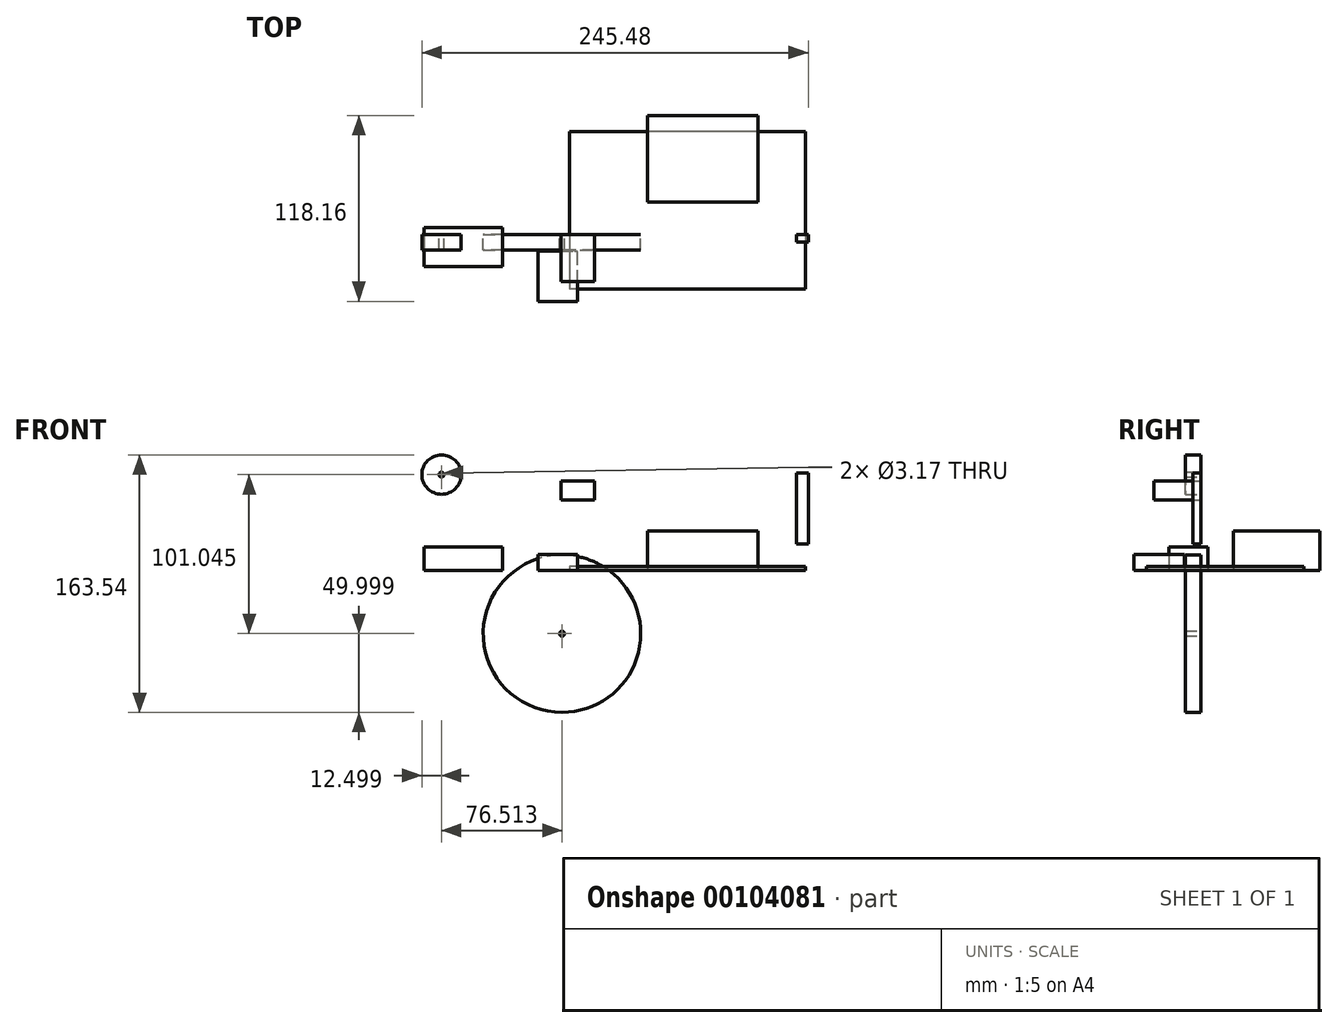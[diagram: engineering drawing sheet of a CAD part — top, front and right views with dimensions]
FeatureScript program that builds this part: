
annotation { "Feature Type Name" : "Feature", "Feature Type Description" : "" }
export const myFeature = defineFeature(function(context is Context, id is Id, definition is map)
    precondition{}
    {
        {
            var Q0;
            Q0=qCreatedBy(makeId("Top.planeOp"),FACE);
            var sketch = newSketch(context, id + "F0", { "sketchPlane" : qUnion([Q0])});
            skLineSegment(sketch, "E0.bottom", {"start": v(-136.78, 4.5) * mm, "end": v(-86.78, 4.5) * mm});
            skLineSegment(sketch, "E0.top", {"start": v(-136.78, -20.5) * mm, "end": v(-86.78, -20.5) * mm});
            skLineSegment(sketch, "E0.left", {"start": v(-136.78, 4.5) * mm, "end": v(-136.78, -20.5) * mm});
            skLineSegment(sketch, "E0.right", {"start": v(-86.78, 4.5) * mm, "end": v(-86.78, -20.5) * mm});
            skSolve(sketch);
        }
        {
            var Q0;
            Q0=makeQuery(id+"F0.imprint","IMPRINT",FACE,{"disambiguationData":[TD([[makeQuery(id+"F0.imprint","IMPRINT",EDGE,{"derivedFrom":sQuery(id+"F0.wireOp",EDGE,"E0.bottom")}),-1.0]])]});
            extrude(context, id + "F1", {"entities" : qUnion([Q0]), "depth" : 15 * mm});
        }
        {
            var Q0;
            Q0=qCreatedBy(makeId("Top.planeOp"),FACE);
            var sketch = newSketch(context, id + "F2", { "sketchPlane" : qUnion([Q0])});
            skLineSegment(sketch, "E1.bottom", {"start": v(5.38, 75.6) * mm, "end": v(75.38, 75.6) * mm});
            skLineSegment(sketch, "E1.top", {"start": v(5.38, 20.6) * mm, "end": v(75.38, 20.6) * mm});
            skLineSegment(sketch, "E1.left", {"start": v(5.38, 75.6) * mm, "end": v(5.38, 20.6) * mm});
            skLineSegment(sketch, "E1.right", {"start": v(75.38, 75.6) * mm, "end": v(75.38, 20.6) * mm});
            skSolve(sketch);
        }
        {
            var Q0;
            Q0=makeQuery(id+"F2.imprint","IMPRINT",FACE,{"disambiguationData":[TD([[makeQuery(id+"F2.imprint","IMPRINT",EDGE,{"derivedFrom":sQuery(id+"F2.wireOp",EDGE,"E1.bottom")}),-1.0]])]});
            extrude(context, id + "F3", {"entities" : qUnion([Q0]), "depth" : 25 * mm});
        }
        {
            var Q0;
            Q0=qCreatedBy(makeId("Front.planeOp"),FACE);
            var sketch = newSketch(context, id + "F4", { "sketchPlane" : qUnion([Q0])});
            skLineSegment(sketch, "E2.bottom", {"start": v(-49.55, 56.88) * mm, "end": v(-28.55, 56.88) * mm});
            skLineSegment(sketch, "E2.top", {"start": v(-49.55, 44.88) * mm, "end": v(-28.55, 44.88) * mm});
            skLineSegment(sketch, "E2.left", {"start": v(-49.55, 56.88) * mm, "end": v(-49.55, 44.88) * mm});
            skLineSegment(sketch, "E2.right", {"start": v(-28.55, 56.88) * mm, "end": v(-28.55, 44.88) * mm});
            skSolve(sketch);
        }
        {
            var Q0;
            Q0=makeQuery(id+"F4.imprint","IMPRINT",FACE,{"disambiguationData":[TD([[makeQuery(id+"F4.imprint","IMPRINT",EDGE,{"derivedFrom":sQuery(id+"F4.wireOp",EDGE,"E2.bottom")}),-1.0]])]});
            extrude(context, id + "F5", {"entities" : qUnion([Q0]), "depth" : 30 * mm});
        }
        {
            var Q0;
            Q0=qCreatedBy(makeId("Top.planeOp"),FACE);
            var sketch = newSketch(context, id + "F6", { "sketchPlane" : qUnion([Q0])});
            skLineSegment(sketch, "E3.bottom", {"start": v(-64.2, -42.57) * mm, "end": v(-39.2, -42.57) * mm});
            skLineSegment(sketch, "E3.top", {"start": v(-64.2, -10.57) * mm, "end": v(-39.2, -10.57) * mm});
            skLineSegment(sketch, "E3.left", {"start": v(-64.2, -42.57) * mm, "end": v(-64.2, -10.57) * mm});
            skLineSegment(sketch, "E3.right", {"start": v(-39.2, -42.57) * mm, "end": v(-39.2, -10.57) * mm});
            skSolve(sketch);
        }
        {
            var Q0;
            Q0=makeQuery(id+"F6.imprint","IMPRINT",FACE,{"disambiguationData":[TD([[makeQuery(id+"F6.imprint","IMPRINT",EDGE,{"derivedFrom":sQuery(id+"F6.wireOp",EDGE,"E3.bottom")}),1.0]])]});
            extrude(context, id + "F7", {"entities" : qUnion([Q0]), "depth" : 10 * mm});
        }
        {
            var Q0;
            Q0=qCreatedBy(makeId("Top.planeOp"),FACE);
            var sketch = newSketch(context, id + "F8", { "sketchPlane" : qUnion([Q0])});
            skLineSegment(sketch, "E4.bottom", {"start": v(105.62, 65.38) * mm, "end": v(-44.38, 65.38) * mm});
            skLineSegment(sketch, "E4.top", {"start": v(105.62, -34.62) * mm, "end": v(-44.38, -34.62) * mm});
            skLineSegment(sketch, "E4.left", {"start": v(105.62, 65.38) * mm, "end": v(105.62, -34.62) * mm});
            skLineSegment(sketch, "E4.right", {"start": v(-44.38, 65.38) * mm, "end": v(-44.38, -34.62) * mm});
            skSolve(sketch);
        }
        {
            var Q0;
            Q0=makeQuery(id+"F8.imprint","IMPRINT",FACE,{"disambiguationData":[TD([[makeQuery(id+"F8.imprint","IMPRINT",EDGE,{"derivedFrom":sQuery(id+"F8.wireOp",EDGE,"E4.bottom")}),1.0]])]});
            extrude(context, id + "F9", {"entities" : qUnion([Q0]), "depth" : 2.5 * mm});
        }
        {
            var Q0;
            Q0=qCreatedBy(makeId("Front.planeOp"),FACE);
            var sketch = newSketch(context, id + "F10", { "sketchPlane" : qUnion([Q0])});
            skCircle(sketch, "E5", {"center": v(-49.08, -40.18) * mm, "radius": 50 * mm});
            skCircle(sketch, "E6", {"center": v(-49.08, -40.18) * mm, "radius": 1.59 * mm});
            skSolve(sketch);
        }
        {
            var Q0;
            Q0=makeQuery(id+"F10.imprint","IMPRINT",FACE,{"disambiguationData":[TD([[makeQuery(id+"F10.imprint","IMPRINT",EDGE,{"derivedFrom":sQuery(id+"F10.wireOp",EDGE,"E5")}),1.0]])]});
            extrude(context, id + "F11", {"entities" : qUnion([Q0]), "depth" : 10 * mm});
        }
        {
            var Q0;
            Q0=qCreatedBy(makeId("Front.planeOp"),FACE);
            var sketch = newSketch(context, id + "F12", { "sketchPlane" : qUnion([Q0])});
            skCircle(sketch, "E7", {"center": v(-125.6, 60.86) * mm, "radius": 12.5 * mm});
            skCircle(sketch, "E8", {"center": v(-125.6, 60.86) * mm, "radius": 1.59 * mm});
            skSolve(sketch);
        }
        {
            var Q0;
            Q0=makeQuery(id+"F12.imprint","IMPRINT",FACE,{"disambiguationData":[TD([[makeQuery(id+"F12.imprint","IMPRINT",EDGE,{"derivedFrom":sQuery(id+"F12.wireOp",EDGE,"E7")}),1.0]])]});
            var Q1;
            Q1 = qSketchRegion(id + "F14", true);
            extrude(context, id + "F13", {"entities" : qUnion([Q0, Q1]), "depth" : 10 * mm});
        }
        {
            var Q0;
            Q0=qCreatedBy(makeId("Front.planeOp"),FACE);
            var sketch = newSketch(context, id + "F14", { "sketchPlane" : qUnion([Q0])});
            skLineSegment(sketch, "E9.bottom", {"start": v(99.89, 61.79) * mm, "end": v(107.39, 61.79) * mm});
            skLineSegment(sketch, "E9.top", {"start": v(99.89, 16.79) * mm, "end": v(107.39, 16.79) * mm});
            skLineSegment(sketch, "E9.left", {"start": v(99.89, 61.79) * mm, "end": v(99.89, 16.79) * mm});
            skLineSegment(sketch, "E9.right", {"start": v(107.39, 61.79) * mm, "end": v(107.39, 16.79) * mm});
            skSolve(sketch);
        }
        {
            var Q0;
            Q0=makeQuery(id+"F14.imprint","IMPRINT",FACE,{"disambiguationData":[TD([[makeQuery(id+"F14.imprint","IMPRINT",EDGE,{"derivedFrom":sQuery(id+"F14.wireOp",EDGE,"E9.bottom")}),-1.0]])]});
            extrude(context, id + "F15", {"entities" : qUnion([Q0]), "depth" : 5 * mm});
        }
    });
